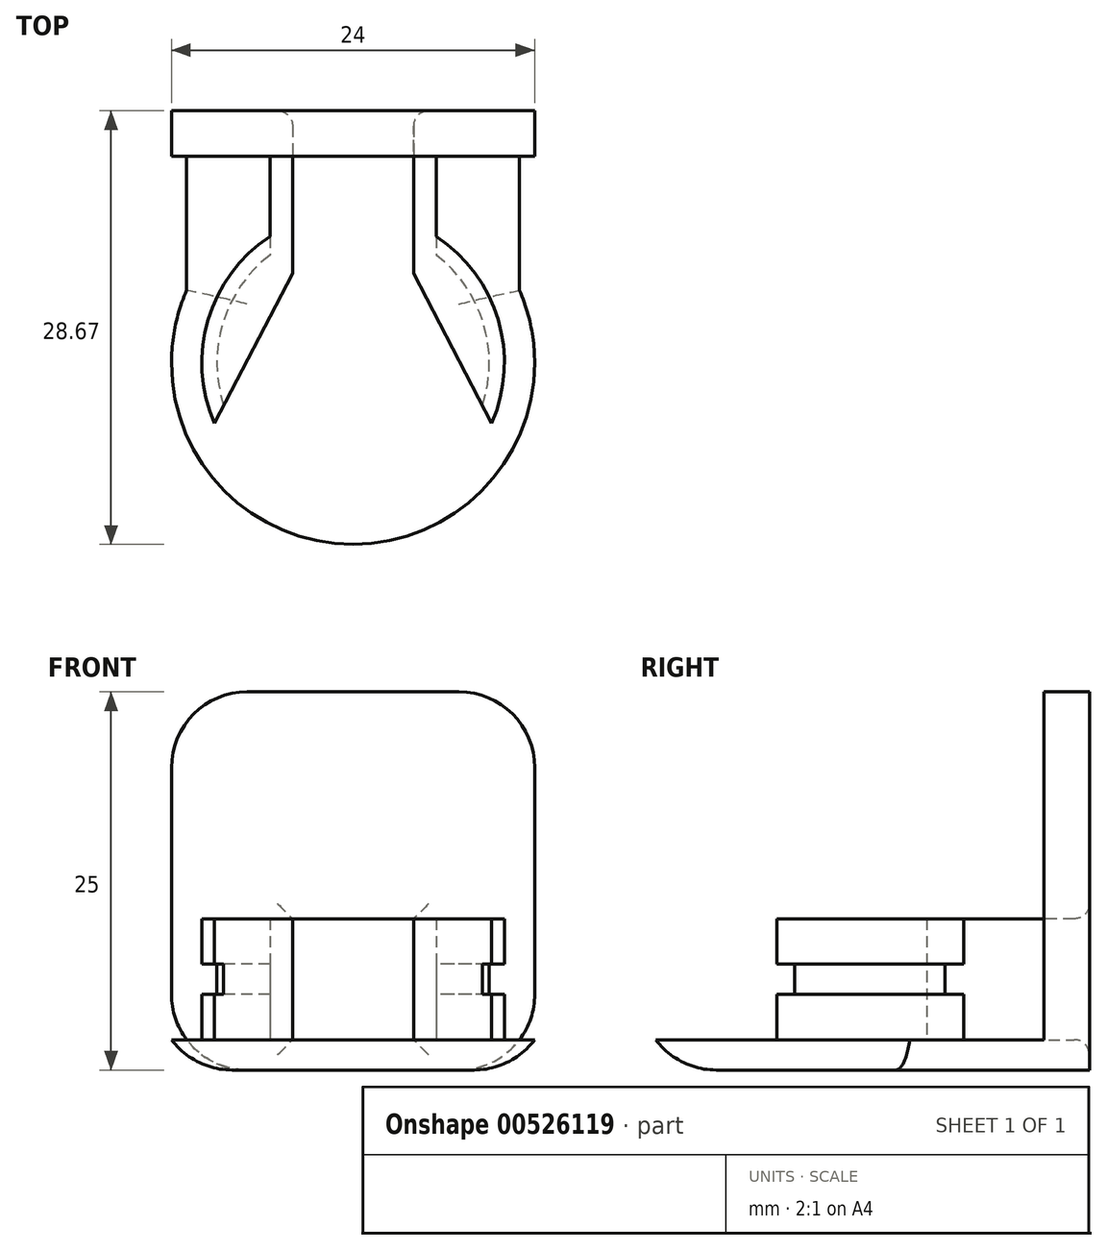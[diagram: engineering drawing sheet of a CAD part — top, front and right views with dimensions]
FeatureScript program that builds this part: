
annotation { "Feature Type Name" : "Feature", "Feature Type Description" : "" }
export const myFeature = defineFeature(function(context is Context, id is Id, definition is map)
    precondition{}
    {
        {
            var Q0;
            Q0=qCreatedBy(makeId("Top.planeOp"),FACE);
            var sketch = newSketch(context, id + "F0", { "sketchPlane" : qUnion([Q0])});
            skArc(sketch, "E0", {"start": v(-5.5, 1.5) * mm, "mid": v(0, 24.17) * mm, "end": v(5.5, 1.5) * mm});
            skArc(sketch, "E1", {"start": v(-5.5, -1.5) * mm, "mid": v(0, -24.17) * mm, "end": v(5.5, -1.5) * mm});
            skLineSegment(sketch, "E2", {"start": v(-5.5, 1.5) * mm, "end": v(-5.5, -1.5) * mm});
            skLineSegment(sketch, "E3", {"start": v(5.5, 1.5) * mm, "end": v(5.5, -1.5) * mm});
            skSolve(sketch);
        }
        {
            var Q0;
            Q0=qSketchRegion(id+"F0",true);
            extrude(context, id + "F1", {"entities" : qUnion([Q0]), "depth" : 2 * mm, "offsetDistance" : 25 * mm});
        }
        {
            var Q0;
            Q0=makeQuery(id+"F1.opExtrude","CAP_FACE",FACE,{"disambiguationData":[OSD([sQuery(id+"F0.wireOp",EDGE,"E0"),sQuery(id+"F0.wireOp",EDGE,"E1"),sQuery(id+"F0.wireOp",EDGE,"E2"),sQuery(id+"F0.wireOp",EDGE,"E3")])],"isStart":false});
            var sketch = newSketch(context, id + "F2", { "sketchPlane" : qUnion([Q0])});
            skArc(sketch, "E4", {"start": v(8.66, 17.17) * mm, "mid": v(9.5, 9.04) * mm, "end": v(4, 3) * mm});
            skArc(sketch, "E5", {"start": v(9.78, 19.11) * mm, "mid": v(11.66, 9.33) * mm, "end": v(5.5, 1.5) * mm});
            skArc(sketch, "E6", {"start": v(-8.66, 17.17) * mm, "mid": v(-9.5, 9.04) * mm, "end": v(-4, 3) * mm});
            skArc(sketch, "E7", {"start": v(5.5, -3.81) * mm, "mid": v(9.59, -9.32) * mm, "end": v(9.17, -16.17) * mm});
            skLineSegment(sketch, "E8", {"start": v(9.78, 19.11) * mm, "end": v(8.66, 17.17) * mm});
            skLineSegment(sketch, "E9", {"start": v(-8.66, 17.17) * mm, "end": v(-9.78, 19.11) * mm});
            skLineSegment(sketch, "E10", {"start": v(5.5, 1.5) * mm, "end": v(5.5, -3.81) * mm});
            skLineSegment(sketch, "E11", {"start": v(-4, 3) * mm, "end": v(-4, -6.24) * mm});
            skLineSegment(sketch, "E12", {"start": v(-4, -6.24) * mm, "end": v(-9.17, -16.17) * mm});
            skLineSegment(sketch, "E13", {"start": v(9.17, -16.17) * mm, "end": v(4, -6.24) * mm});
            skLineSegment(sketch, "E14", {"start": v(4, -6.24) * mm, "end": v(4, 3) * mm});
            skArc(sketch, "E15", {"start": v(-9.78, 19.11) * mm, "mid": v(-11.66, 9.33) * mm, "end": v(-5.5, 1.5) * mm});
            skArc(sketch, "E16", {"start": v(-9.17, -16.17) * mm, "mid": v(-9.59, -9.32) * mm, "end": v(-5.5, -3.81) * mm});
            skLineSegment(sketch, "E17", {"start": v(-5.5, 1.5) * mm, "end": v(-5.5, -3.81) * mm});
            skArc(sketch, "E18.0", {"start": v(-5.5, 1.5) * mm, "mid": v(0, 24.17) * mm, "end": v(5.5, 1.5) * mm, "construction": true});
            skArc(sketch, "E19.0", {"start": v(-5.5, -1.5) * mm, "mid": v(0, -24.17) * mm, "end": v(5.5, -1.5) * mm, "construction": true});
            skSolve(sketch);
        }
        {
            var Q0;
            Q0=qSketchRegion(id+"F2",true);
            extrude(context, id + "F3", {"entities" : qUnion([Q0]), "operationType" : NewBodyOperationType.ADD, "depth" : 3 * mm, "offsetDistance" : 25 * mm});
        }
        {
            var Q0;
            Q0=makeQuery(id+"F3.opExtrude","CAP_FACE",FACE,{"disambiguationData":[OSD([sQuery(id+"F2.wireOp",EDGE,"E4"),sQuery(id+"F2.wireOp",EDGE,"E5"),sQuery(id+"F2.wireOp",EDGE,"E7"),sQuery(id+"F2.wireOp",EDGE,"E8"),sQuery(id+"F2.wireOp",EDGE,"E10"),sQuery(id+"F2.wireOp",EDGE,"E13"),sQuery(id+"F2.wireOp",EDGE,"E14")])],"isStart":false});
            var sketch = newSketch(context, id + "F4", { "sketchPlane" : qUnion([Q0])});
            skArc(sketch, "E20", {"start": v(-9.78, 19.11) * mm, "mid": v(-11.66, 9.33) * mm, "end": v(-5.5, 1.5) * mm});
            skArc(sketch, "E21", {"start": v(9.78, 19.11) * mm, "mid": v(11.66, 9.33) * mm, "end": v(5.5, 1.5) * mm});
            skArc(sketch, "E22", {"start": v(8.07, 16.15) * mm, "mid": v(8.53, 9.28) * mm, "end": v(4, 4.1) * mm});
            skArc(sketch, "E23", {"start": v(-8.07, 16.15) * mm, "mid": v(-8.53, 9.28) * mm, "end": v(-4, 4.1) * mm});
            skArc(sketch, "E24", {"start": v(5.5, -5.04) * mm, "mid": v(8.6, -9.53) * mm, "end": v(8.55, -14.98) * mm});
            skArc(sketch, "E25", {"start": v(-5.5, -5.04) * mm, "mid": v(-8.6, -9.53) * mm, "end": v(-8.55, -14.98) * mm});
            skLineSegment(sketch, "E26", {"start": v(-5.5, 1.5) * mm, "end": v(-5.5, -5.04) * mm});
            skLineSegment(sketch, "E27", {"start": v(5.5, 1.5) * mm, "end": v(5.5, -5.04) * mm});
            skLineSegment(sketch, "E28", {"start": v(-4, 4.1) * mm, "end": v(-4, -6.24) * mm});
            skLineSegment(sketch, "E29", {"start": v(-4, -6.24) * mm, "end": v(-8.55, -14.98) * mm});
            skLineSegment(sketch, "E30", {"start": v(4, 4.1) * mm, "end": v(4, -6.24) * mm});
            skLineSegment(sketch, "E31", {"start": v(4, -6.24) * mm, "end": v(8.55, -14.98) * mm});
            skLineSegment(sketch, "E32", {"start": v(8.07, 16.15) * mm, "end": v(9.78, 19.11) * mm});
            skLineSegment(sketch, "E33", {"start": v(-9.78, 19.11) * mm, "end": v(-8.07, 16.15) * mm});
            skLineSegment(sketch, "E34.0", {"start": v(-8.66, 17.17) * mm, "end": v(-9.78, 19.11) * mm, "construction": true});
            skLineSegment(sketch, "E35.0", {"start": v(9.78, 19.11) * mm, "end": v(8.66, 17.17) * mm, "construction": true});
            skLineSegment(sketch, "E36.0", {"start": v(-4, -6.24) * mm, "end": v(-9.17, -16.17) * mm, "construction": true});
            skLineSegment(sketch, "E37.0", {"start": v(9.17, -16.17) * mm, "end": v(4, -6.24) * mm, "construction": true});
            skArc(sketch, "E38.0", {"start": v(-9.78, 19.11) * mm, "mid": v(0, 24.17) * mm, "end": v(9.78, 19.11) * mm, "construction": true});
            skArc(sketch, "E39.0", {"start": v(-5.5, -1.5) * mm, "mid": v(0, -24.17) * mm, "end": v(5.5, -1.5) * mm, "construction": true});
            skSolve(sketch);
        }
        {
            var Q0;
            Q0=qSketchRegion(id+"F4",true);
            extrude(context, id + "F5", {"entities" : qUnion([Q0]), "operationType" : NewBodyOperationType.ADD, "depth" : 2 * mm, "offsetDistance" : 25 * mm});
        }
        {
            var Q0;
            Q0=makeQuery(id+"F5.opExtrude","CAP_FACE",FACE,{"disambiguationData":[OSD([sQuery(id+"F4.wireOp",EDGE,"E21"),sQuery(id+"F4.wireOp",EDGE,"E22"),sQuery(id+"F4.wireOp",EDGE,"E24"),sQuery(id+"F4.wireOp",EDGE,"E27"),sQuery(id+"F4.wireOp",EDGE,"E30"),sQuery(id+"F4.wireOp",EDGE,"E31"),sQuery(id+"F4.wireOp",EDGE,"E32")])],"isStart":false});
            var sketch = newSketch(context, id + "F6", { "sketchPlane" : qUnion([Q0])});
            skArc(sketch, "E40", {"start": v(8.66, 17.17) * mm, "mid": v(9.5, 9.04) * mm, "end": v(4, 3) * mm});
            skArc(sketch, "E41", {"start": v(9.78, 19.11) * mm, "mid": v(11.66, 9.33) * mm, "end": v(5.5, 1.5) * mm});
            skArc(sketch, "E42", {"start": v(-8.66, 17.17) * mm, "mid": v(-9.5, 9.04) * mm, "end": v(-4, 3) * mm});
            skArc(sketch, "E43", {"start": v(5.5, -3.81) * mm, "mid": v(9.59, -9.32) * mm, "end": v(9.17, -16.17) * mm});
            skLineSegment(sketch, "E44", {"start": v(9.78, 19.11) * mm, "end": v(8.66, 17.17) * mm});
            skLineSegment(sketch, "E45", {"start": v(-8.66, 17.17) * mm, "end": v(-9.78, 19.11) * mm});
            skLineSegment(sketch, "E46", {"start": v(5.5, 1.5) * mm, "end": v(5.5, -3.81) * mm});
            skLineSegment(sketch, "E47", {"start": v(-4, 3) * mm, "end": v(-4, -6.24) * mm});
            skLineSegment(sketch, "E48", {"start": v(-4, -6.24) * mm, "end": v(-9.17, -16.17) * mm});
            skLineSegment(sketch, "E49", {"start": v(9.17, -16.17) * mm, "end": v(4, -6.24) * mm});
            skLineSegment(sketch, "E50", {"start": v(4, -6.24) * mm, "end": v(4, 3) * mm});
            skArc(sketch, "E51", {"start": v(-9.78, 19.11) * mm, "mid": v(-11.66, 9.33) * mm, "end": v(-5.5, 1.5) * mm});
            skArc(sketch, "E52", {"start": v(-9.17, -16.17) * mm, "mid": v(-9.59, -9.32) * mm, "end": v(-5.5, -3.81) * mm});
            skLineSegment(sketch, "E53", {"start": v(-5.5, 1.5) * mm, "end": v(-5.5, -3.81) * mm});
            skArc(sketch, "E54.0", {"start": v(-5.5, -1.5) * mm, "mid": v(0, -24.17) * mm, "end": v(5.5, -1.5) * mm, "construction": true});
            skArc(sketch, "E55.0", {"start": v(-9.78, 19.11) * mm, "mid": v(0, 24.17) * mm, "end": v(9.78, 19.11) * mm, "construction": true});
            skSolve(sketch);
        }
        {
            var Q0;
            Q0=qSketchRegion(id+"F6",true);
            extrude(context, id + "F7", {"entities" : qUnion([Q0]), "operationType" : NewBodyOperationType.ADD, "depth" : 3 * mm, "offsetDistance" : 25 * mm});
        }
        {
            var Q0;
            Q0=makeQuery(id+"F5.opExtrude","CAP_EDGE",EDGE,{"disambiguationData":[OSD([sQuery(id+"F4.wireOp",EDGE,"E22")])],"isStart":false});
            var Q1;
            Q1=makeQuery(id+"F5.opExtrude","CAP_EDGE",EDGE,{"disambiguationData":[OSD([sQuery(id+"F4.wireOp",EDGE,"E23")])],"isStart":false});
            var Q2;
            Q2=makeQuery(id+"F5.opExtrude","CAP_EDGE",EDGE,{"disambiguationData":[OSD([sQuery(id+"F4.wireOp",EDGE,"E23")])],"isStart":true});
            var Q3;
            Q3=makeQuery(id+"F5.opExtrude","CAP_EDGE",EDGE,{"disambiguationData":[OSD([sQuery(id+"F4.wireOp",EDGE,"E22")])],"isStart":true});
            var Q4;
            Q4=makeQuery(id+"F5.opExtrude","CAP_EDGE",EDGE,{"disambiguationData":[OSD([sQuery(id+"F4.wireOp",EDGE,"E25")])],"isStart":true});
            var Q5;
            Q5=makeQuery(id+"F5.opExtrude","CAP_EDGE",EDGE,{"disambiguationData":[OSD([sQuery(id+"F4.wireOp",EDGE,"E25")])],"isStart":false});
            var Q6;
            Q6=makeQuery(id+"F5.opExtrude","CAP_EDGE",EDGE,{"disambiguationData":[OSD([sQuery(id+"F4.wireOp",EDGE,"E24")])],"isStart":false});
            var Q7;
            Q7=makeQuery(id+"F5.opExtrude","CAP_EDGE",EDGE,{"disambiguationData":[OSD([sQuery(id+"F4.wireOp",EDGE,"E24")])],"isStart":true});
            fillet(context, id + "F8", {"entities" : qUnion([Q0, Q1, Q2, Q3, Q4, Q5, Q6, Q7]), "radius" : 1 * mm, "tangentPropagation" : true, "allowEdgeOverflow" : false});
        }
        {
            var Q0;
            Q0=makeQuery(id+"F7.opExtrude","CAP_FACE",FACE,{"disambiguationData":[OSD([sQuery(id+"F6.wireOp",EDGE,"E40"),sQuery(id+"F6.wireOp",EDGE,"E41"),sQuery(id+"F6.wireOp",EDGE,"E43"),sQuery(id+"F6.wireOp",EDGE,"E44"),sQuery(id+"F6.wireOp",EDGE,"E46"),sQuery(id+"F6.wireOp",EDGE,"E49"),sQuery(id+"F6.wireOp",EDGE,"E50")])],"isStart":false});
            var sketch = newSketch(context, id + "F9", { "sketchPlane" : qUnion([Q0])});
            skLineSegment(sketch, "E56.bottom", {"start": v(-12, 1.5) * mm, "end": v(12, 1.5) * mm});
            skLineSegment(sketch, "E56.top", {"start": v(-12, 24.17) * mm, "end": v(12, 24.17) * mm});
            skLineSegment(sketch, "E56.left", {"start": v(-12, 24.17) * mm, "end": v(-12, 1.5) * mm});
            skLineSegment(sketch, "E56.right", {"start": v(12, 24.17) * mm, "end": v(12, 1.5) * mm});
            skSolve(sketch);
        }
        {
            var Q0;
            Q0=qSketchRegion(id+"F9",true);
            extrude(context, id + "F10", {"entities" : qUnion([Q0]), "operationType" : NewBodyOperationType.REMOVE, "oppositeDirection" : true, "depth" : 10 * mm, "offsetDistance" : 25 * mm});
        }
        {
            var Q0;
            Q0=makeQuery(id+"F10.boolean.opBoolean","COPY",FACE,{"derivedFrom":makeQuery(id+"F10.opExtrude","SWEPT_FACE",FACE,{"disambiguationData":[OSD([sQuery(id+"F9.wireOp",EDGE,"E56.bottom")])]})});
            var sketch = newSketch(context, id + "F11", { "sketchPlane" : qUnion([Q0])});
            skLineSegment(sketch, "E57.bottom", {"start": v(-12, 25) * mm, "end": v(12, 25) * mm});
            skLineSegment(sketch, "E57.top", {"start": v(-12, 0) * mm, "end": v(12, 0) * mm});
            skLineSegment(sketch, "E57.left", {"start": v(-12, 25) * mm, "end": v(-12, 0) * mm});
            skLineSegment(sketch, "E57.right", {"start": v(12, 25) * mm, "end": v(12, 0) * mm});
            skLineSegment(sketch, "E58.bottom", {"start": v(-4, 10) * mm, "end": v(4, 10) * mm});
            skLineSegment(sketch, "E58.top", {"start": v(-4, 2) * mm, "end": v(4, 2) * mm});
            skLineSegment(sketch, "E58.left", {"start": v(4, 10) * mm, "end": v(4, 2) * mm});
            skLineSegment(sketch, "E58.right", {"start": v(-4, 10) * mm, "end": v(-4, 2) * mm});
            skSolve(sketch);
        }
        {
            var Q0;
            Q0=qSketchRegion(id+"F11",true);
            extrude(context, id + "F12", {"entities" : qUnion([Q0]), "operationType" : NewBodyOperationType.ADD, "depth" : 3 * mm, "offsetDistance" : 25 * mm});
        }
        {
            var Q0;
            Q0=makeQuery(id+"F12.opExtrude","CAP_EDGE",EDGE,{"disambiguationData":[OSD([sQuery(id+"F11.wireOp",EDGE,"E58.bottom")])],"isStart":false});
            var Q1;
            Q1=makeQuery(id+"F12.opExtrude","CAP_EDGE",EDGE,{"disambiguationData":[OSD([sQuery(id+"F11.wireOp",EDGE,"E58.right")])],"isStart":false});
            var Q2;
            Q2=makeQuery(id+"F12.opExtrude","CAP_EDGE",EDGE,{"disambiguationData":[OSD([sQuery(id+"F11.wireOp",EDGE,"E58.top")])],"isStart":false});
            var Q3;
            Q3=makeQuery(id+"F12.opExtrude","CAP_EDGE",EDGE,{"disambiguationData":[OSD([sQuery(id+"F11.wireOp",EDGE,"E58.left")])],"isStart":false});
            fillet(context, id + "F13", {"entities" : qUnion([Q0, Q1, Q2, Q3]), "radius" : 1 * mm, "tangentPropagation" : true, "allowEdgeOverflow" : false});
        }
        {
            var Q0;
            Q0=makeQuery(id+"F12.boolean.opBoolean","MERGE",FACE,{"derivedFrom":[makeQuery(id+"F1.opExtrude","CAP_FACE",FACE,{"disambiguationData":[OSD([sQuery(id+"F0.wireOp",EDGE,"E0"),sQuery(id+"F0.wireOp",EDGE,"E1"),sQuery(id+"F0.wireOp",EDGE,"E2"),sQuery(id+"F0.wireOp",EDGE,"E3")])],"isStart":true}),makeQuery(id+"F12.opExtrude","SWEPT_FACE",FACE,{"disambiguationData":[OSD([sQuery(id+"F11.wireOp",EDGE,"E57.top")])]})]});
            var sketch = newSketch(context, id + "F14", { "sketchPlane" : qUnion([Q0])});
            skLineSegment(sketch, "E59.bottom", {"start": v(-12, -1.5) * mm, "end": v(12, -1.5) * mm});
            skLineSegment(sketch, "E59.top", {"start": v(-12, 12.17) * mm, "end": v(12, 12.17) * mm});
            skLineSegment(sketch, "E59.left", {"start": v(12, 12.17) * mm, "end": v(12, -1.5) * mm});
            skLineSegment(sketch, "E59.right", {"start": v(-12, 12.17) * mm, "end": v(-12, -1.5) * mm});
            skSolve(sketch);
        }
        {
            var Q0;
            Q0=qSketchRegion(id+"F14",true);
            extrude(context, id + "F15", {"entities" : qUnion([Q0]), "operationType" : NewBodyOperationType.ADD, "oppositeDirection" : true, "depth" : 2 * mm, "offsetDistance" : 25 * mm});
        }
        {
            var Q0;
            Q0=makeQuery(id+"F12.opExtrude","SWEPT_EDGE",EDGE,{"disambiguationData":[OSD([sQuery(id+"F11.wireOp",EDGE,"E57.bottom"),sQuery(id+"F11.wireOp",EDGE,"E57.left")])]});
            var Q1;
            Q1=makeQuery(id+"F12.opExtrude","SWEPT_EDGE",EDGE,{"disambiguationData":[OSD([sQuery(id+"F11.wireOp",EDGE,"E57.bottom"),sQuery(id+"F11.wireOp",EDGE,"E57.right")])]});
            var Q2;
            Q2=makeQuery(id+"F15.boolean.opBoolean","MERGE",EDGE,{"derivedFrom":[makeQuery(id+"F12.opExtrude","SWEPT_EDGE",EDGE,{"disambiguationData":[OSD([sQuery(id+"F11.wireOp",EDGE,"E57.top"),sQuery(id+"F11.wireOp",EDGE,"E57.right")])]}),makeQuery(id+"F15.opExtrude","CAP_EDGE",EDGE,{"disambiguationData":[OSD([sQuery(id+"F14.wireOp",EDGE,"E59.right")])],"isStart":true})]});
            fillet(context, id + "F16", {"entities" : qUnion([Q0, Q1, Q2]), "radius" : 5 * mm, "tangentPropagation" : true, "allowEdgeOverflow" : false});
        }
    });
